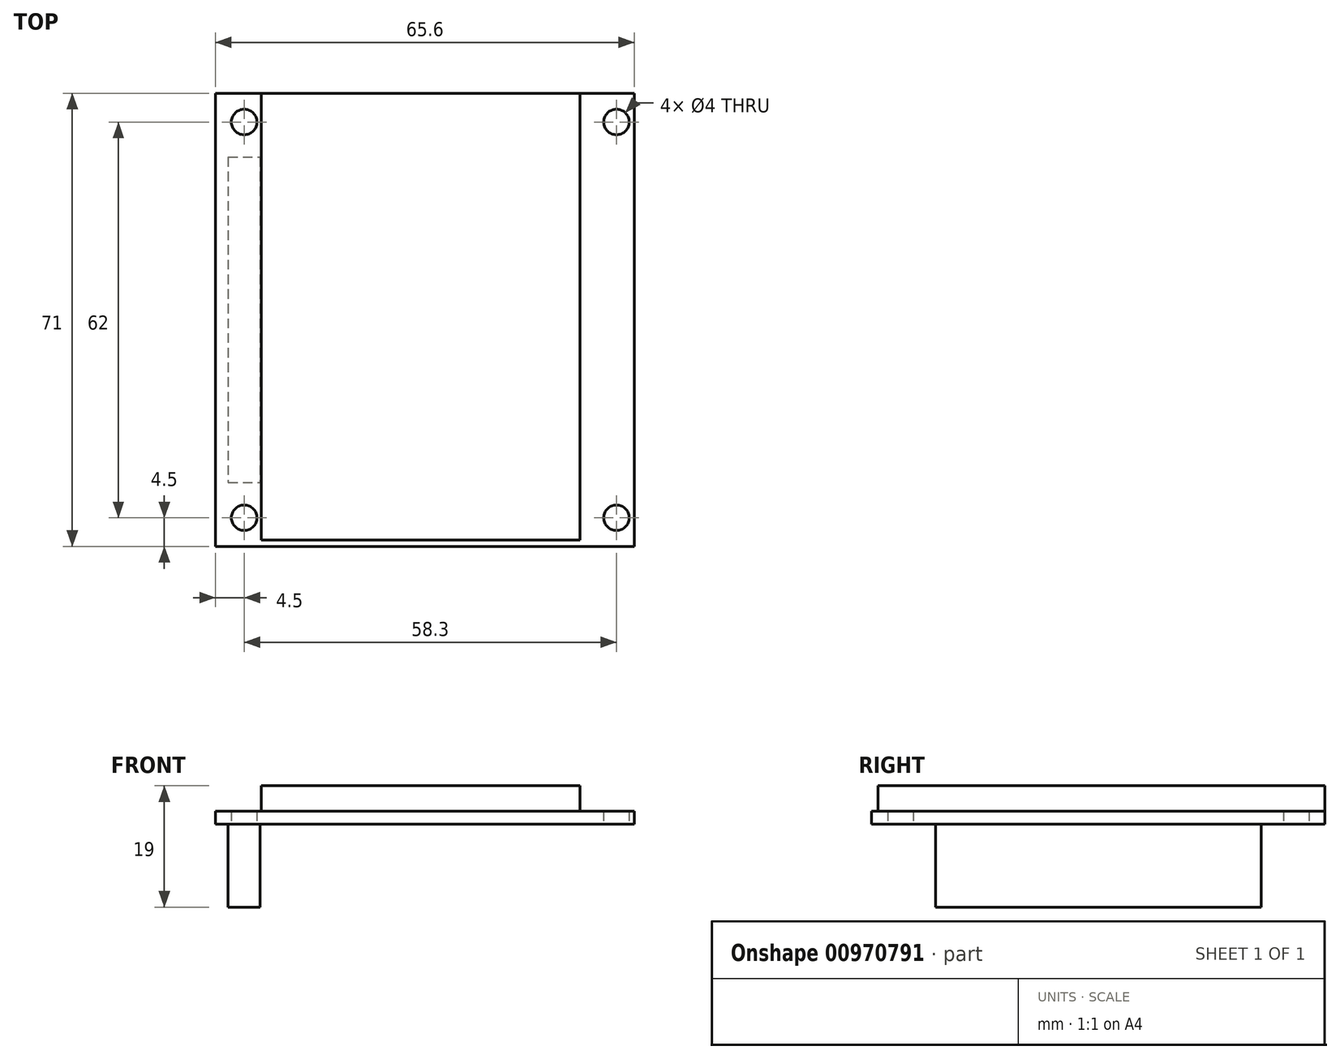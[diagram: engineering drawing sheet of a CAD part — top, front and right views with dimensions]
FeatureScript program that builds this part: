
annotation { "Feature Type Name" : "Feature", "Feature Type Description" : "" }
export const myFeature = defineFeature(function(context is Context, id is Id, definition is map)
    precondition{}
    {
        {
            var Q0;
            Q0=qCreatedBy(makeId("Top.planeOp"),FACE);
            var sketch = newSketch(context, id + "F0", { "sketchPlane" : qUnion([Q0])});
            skLineSegment(sketch, "E0.bottom", {"start": v(-32.8, 35.5) * mm, "end": v(32.8, 35.5) * mm});
            skLineSegment(sketch, "E0.top", {"start": v(-32.8, -35.5) * mm, "end": v(32.8, -35.5) * mm});
            skLineSegment(sketch, "E0.left", {"start": v(-32.8, 35.5) * mm, "end": v(-32.8, -35.5) * mm});
            skLineSegment(sketch, "E0.right", {"start": v(32.8, 35.5) * mm, "end": v(32.8, -35.5) * mm});
            skPoint(sketch, "E0.middle", {"position": v(0, 0) * mm});
            skLineSegment(sketch, "E1.bottom", {"start": v(-25.6, 35.5) * mm, "end": v(24.3, 35.5) * mm});
            skLineSegment(sketch, "E1.top", {"start": v(-25.6, -34.5) * mm, "end": v(24.3, -34.5) * mm});
            skLineSegment(sketch, "E1.left", {"start": v(-25.6, 35.5) * mm, "end": v(-25.6, -34.5) * mm});
            skLineSegment(sketch, "E1.right", {"start": v(24.3, 35.5) * mm, "end": v(24.3, -34.5) * mm});
            skCircle(sketch, "E2", {"center": v(-28.3, 31) * mm, "radius": 2 * mm});
            skCircle(sketch, "E3", {"center": v(-28.3, -31) * mm, "radius": 2 * mm});
            skCircle(sketch, "E4", {"center": v(30, -31) * mm, "radius": 2 * mm});
            skCircle(sketch, "E5", {"center": v(30, 31) * mm, "radius": 2 * mm});
            skLineSegment(sketch, "E6.bottom", {"start": v(-30.8, 25.5) * mm, "end": v(-25.8, 25.5) * mm});
            skLineSegment(sketch, "E6.top", {"start": v(-30.8, -25.5) * mm, "end": v(-25.8, -25.5) * mm});
            skLineSegment(sketch, "E6.left", {"start": v(-30.8, 25.5) * mm, "end": v(-30.8, -25.5) * mm});
            skLineSegment(sketch, "E6.right", {"start": v(-25.8, 25.5) * mm, "end": v(-25.8, -25.5) * mm});
            skPoint(sketch, "E6.middle", {"position": v(-28.3, 0) * mm});
            skSolve(sketch);
        }
        {
            var Q0;
            Q0=makeQuery(id+"F0.imprint","IMPRINT",FACE,{"disambiguationData":[TD([[makeQuery(id+"F0.imprint","IMPRINT",EDGE,{"derivedFrom":sQuery(id+"F0.wireOp",EDGE,"E0.top")}),1.0]])]});
            var Q1;
            Q1=makeQuery(id+"F0.imprint","IMPRINT",FACE,{"disambiguationData":[TD([[makeQuery(id+"F0.imprint","IMPRINT",EDGE,{"derivedFrom":sQuery(id+"F0.wireOp",EDGE,"E1.top")}),1.0]])]});
            var Q2;
            Q2=makeQuery(id+"F0.imprint","IMPRINT",FACE,{"disambiguationData":[TD([[makeQuery(id+"F0.imprint","IMPRINT",EDGE,{"derivedFrom":sQuery(id+"F0.wireOp",EDGE,"E6.bottom")}),-1.0]])]});
            extrude(context, id + "F1", {"entities" : qUnion([Q0, Q1, Q2]), "surfaceOperationType" : NewSurfaceOperationType.ADD, "depth" : 2 * mm, "offsetDistance" : 25 * mm});
        }
        {
            var Q0;
            Q0=makeQuery(id+"F0.imprint","IMPRINT",FACE,{"disambiguationData":[TD([[makeQuery(id+"F0.imprint","IMPRINT",EDGE,{"derivedFrom":sQuery(id+"F0.wireOp",EDGE,"E1.top")}),1.0]])]});
            extrude(context, id + "F2", {"entities" : qUnion([Q0]), "operationType" : NewBodyOperationType.ADD, "depth" : 6 * mm, "offsetDistance" : 25 * mm});
        }
        {
            var Q0;
            Q0=makeQuery(id+"F0.imprint","IMPRINT",FACE,{"disambiguationData":[TD([[makeQuery(id+"F0.imprint","IMPRINT",EDGE,{"derivedFrom":sQuery(id+"F0.wireOp",EDGE,"E6.bottom")}),-1.0]])]});
            extrude(context, id + "F3", {"entities" : qUnion([Q0]), "operationType" : NewBodyOperationType.ADD, "oppositeDirection" : true, "depth" : 13 * mm, "offsetDistance" : 25 * mm});
        }
    });
